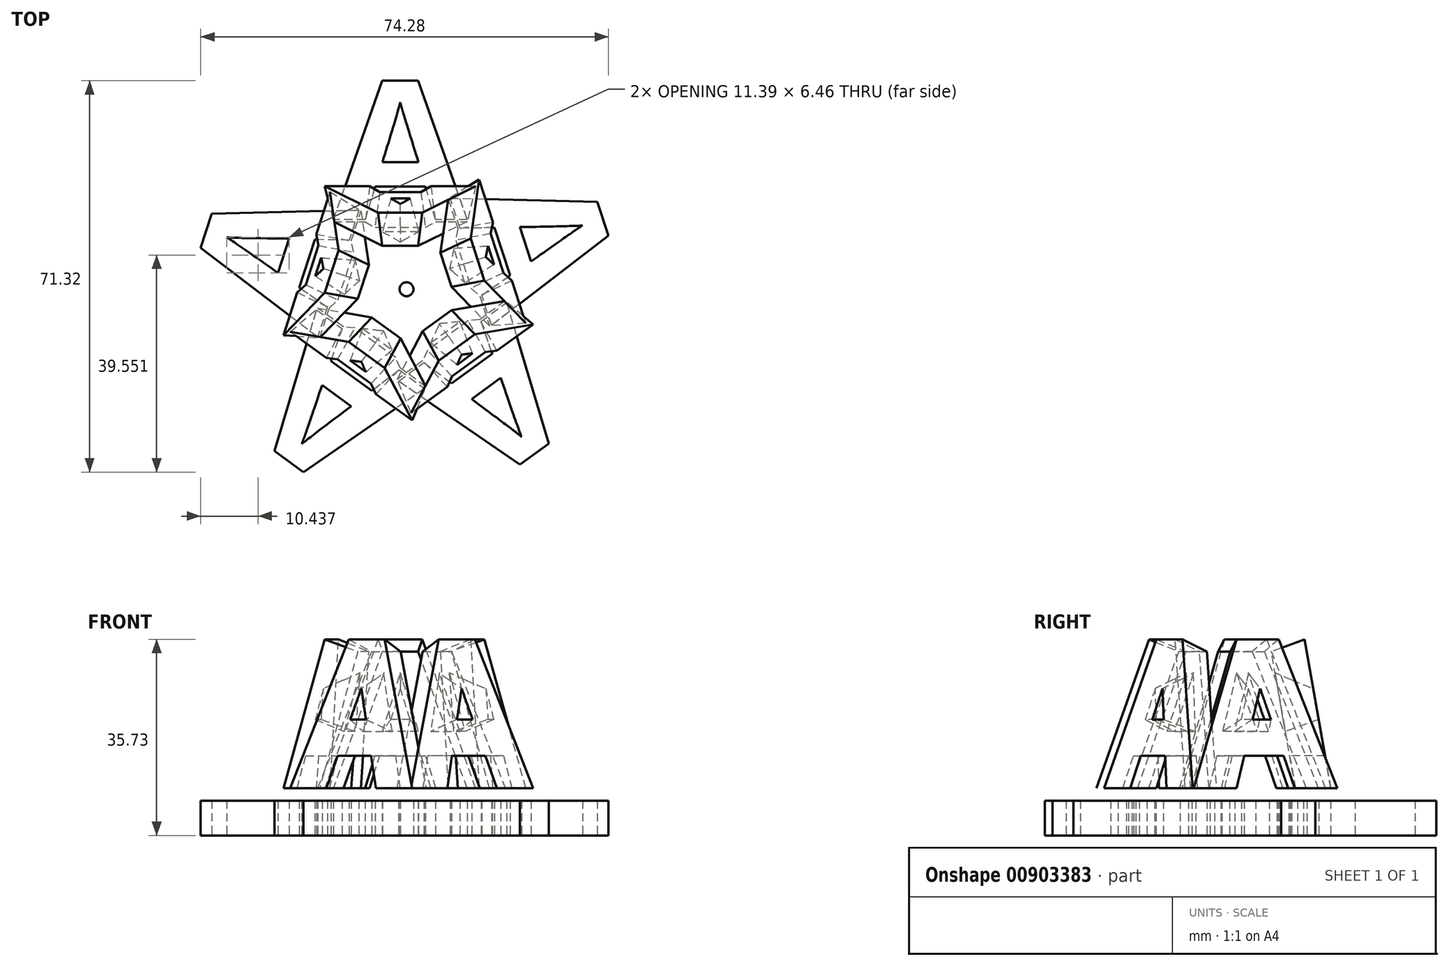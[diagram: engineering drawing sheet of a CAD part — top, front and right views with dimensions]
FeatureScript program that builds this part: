
annotation { "Feature Type Name" : "Feature", "Feature Type Description" : "" }
export const myFeature = defineFeature(function(context is Context, id is Id, definition is map)
    precondition{}
    {
        {
            var Q0;
            Q0=qCreatedBy(makeId("Top.planeOp"),FACE);
            var sketch = newSketch(context, id + "F0", { "sketchPlane" : qUnion([Q0])});
            skText(sketch, "E0", { "text": "A", "fontName": "OpenSans-Bold.ttf"});
            skCircle(sketch, "E1", {"center": v(0, 0) * mm, "radius": 1.27 * mm});
            const initialGuessF0  = {"E0": [-0.01331, 0.0127, 1, 0, 0.0254]};
            skSetInitialGuess(sketch, initialGuessF0);
            skSolve(sketch);
        }
        {
            var Q0;
            Q0 = qSketchRegion(id + "F0", true);
            extrude(context, id + "F1", {"entities" : qUnion([Q0]), "depth" : 6.35 * mm, "offsetDistance" : 25.4 * mm});
        }
        {
            var Q0;
            Q0=makeQuery(id+"F1.opExtrude","CAP_EDGE",EDGE,{"disambiguationData":[OSD([sQuery(id+"F0.wireOp",EDGE,"E0.sketch_text.stroke-3")])],"isStart":false});
            cPlane(context, id + "F2", {"entities" : qUnion([Q0]), "cplaneType" : CPlaneType.LINE_ANGLE, "offset" : 25.4 * mm, "angle" : 10 * degree, "oppositeDirection" : true, "width" : 152.4 * mm, "height" : 152.4 * mm});
        }
        {
            var Q0;
            Q0=qCreatedBy(id+"F2.planeOp",FACE);
            var sketch = newSketch(context, id + "F3", { "sketchPlane" : qUnion([Q0])});
            skText(sketch, "E2", { "text": "A", "fontName": "OpenSans-Bold.ttf"});
            const initialGuessF3  = {"E2": [-0.01331, 0.00635, 1, 0, 0.0254]};
            skSetInitialGuess(sketch, initialGuessF3);
            skSolve(sketch);
        }
        {
            var Q0;
            Q0 = qSketchRegion(id + "F3", true);
            extrude(context, id + "F4", {"entities" : qUnion([Q0]), "operationType" : NewBodyOperationType.ADD, "oppositeDirection" : true, "depth" : 6.35 * mm, "offsetDistance" : 25.4 * mm, "hasDraft" : true, "draftAngle" : 10 * degree});
        }
        {
            var Q0;
            Q0=makeQuery(id+"F1.opExtrude","SWEPT_BODY",BODY,{"disambiguationData":[OSD([sQuery(id+"F0.wireOp",EDGE,"E0.sketch_text.stroke-0"),sQuery(id+"F0.wireOp",EDGE,"E0.sketch_text.stroke-1"),sQuery(id+"F0.wireOp",EDGE,"E0.sketch_text.stroke-2"),sQuery(id+"F0.wireOp",EDGE,"E0.sketch_text.stroke-3"),sQuery(id+"F0.wireOp",EDGE,"E0.sketch_text.stroke-4"),sQuery(id+"F0.wireOp",EDGE,"E0.sketch_text.stroke-5"),sQuery(id+"F0.wireOp",EDGE,"E0.sketch_text.stroke-6"),sQuery(id+"F0.wireOp",EDGE,"E0.sketch_text.stroke-7"),sQuery(id+"F0.wireOp",EDGE,"E0.sketch_text.stroke-8"),sQuery(id+"F0.wireOp",EDGE,"E0.sketch_text.stroke-9"),sQuery(id+"F0.wireOp",EDGE,"E0.sketch_text.stroke-10"),sQuery(id+"F0.wireOp",EDGE,"E0.sketch_text.stroke-11")])]});
            var Q1;
            Q1=makeQuery(id+"F4.opExtrude","SWEPT_BODY",BODY,{"disambiguationData":[OSD([sQuery(id+"F3.wireOp",EDGE,"E2.sketch_text.stroke-0"),sQuery(id+"F3.wireOp",EDGE,"E2.sketch_text.stroke-1"),sQuery(id+"F3.wireOp",EDGE,"E2.sketch_text.stroke-2"),sQuery(id+"F3.wireOp",EDGE,"E2.sketch_text.stroke-3"),sQuery(id+"F3.wireOp",EDGE,"E2.sketch_text.stroke-4"),sQuery(id+"F3.wireOp",EDGE,"E2.sketch_text.stroke-5"),sQuery(id+"F3.wireOp",EDGE,"E2.sketch_text.stroke-6"),sQuery(id+"F3.wireOp",EDGE,"E2.sketch_text.stroke-7"),sQuery(id+"F3.wireOp",EDGE,"E2.sketch_text.stroke-8"),sQuery(id+"F3.wireOp",EDGE,"E2.sketch_text.stroke-9"),sQuery(id+"F3.wireOp",EDGE,"E2.sketch_text.stroke-10"),sQuery(id+"F3.wireOp",EDGE,"E2.sketch_text.stroke-11")])]});
            var Q2;
            Q2=makeQuery(id+"F1.opExtrude","CAP_EDGE",EDGE,{"disambiguationData":[OSD([sQuery(id+"F0.wireOp",EDGE,"E1")])],"isStart":false});
            circularPattern(context, id + "F5", {"operationType" : NewBodyOperationType.ADD, "entities" : qUnion([Q0, Q1]), "axis" : qUnion([Q2]), "angle" : 360 * degree, "instanceCount" : 5, "equalSpace" : true, "isCentered" : true});
        }
    });
